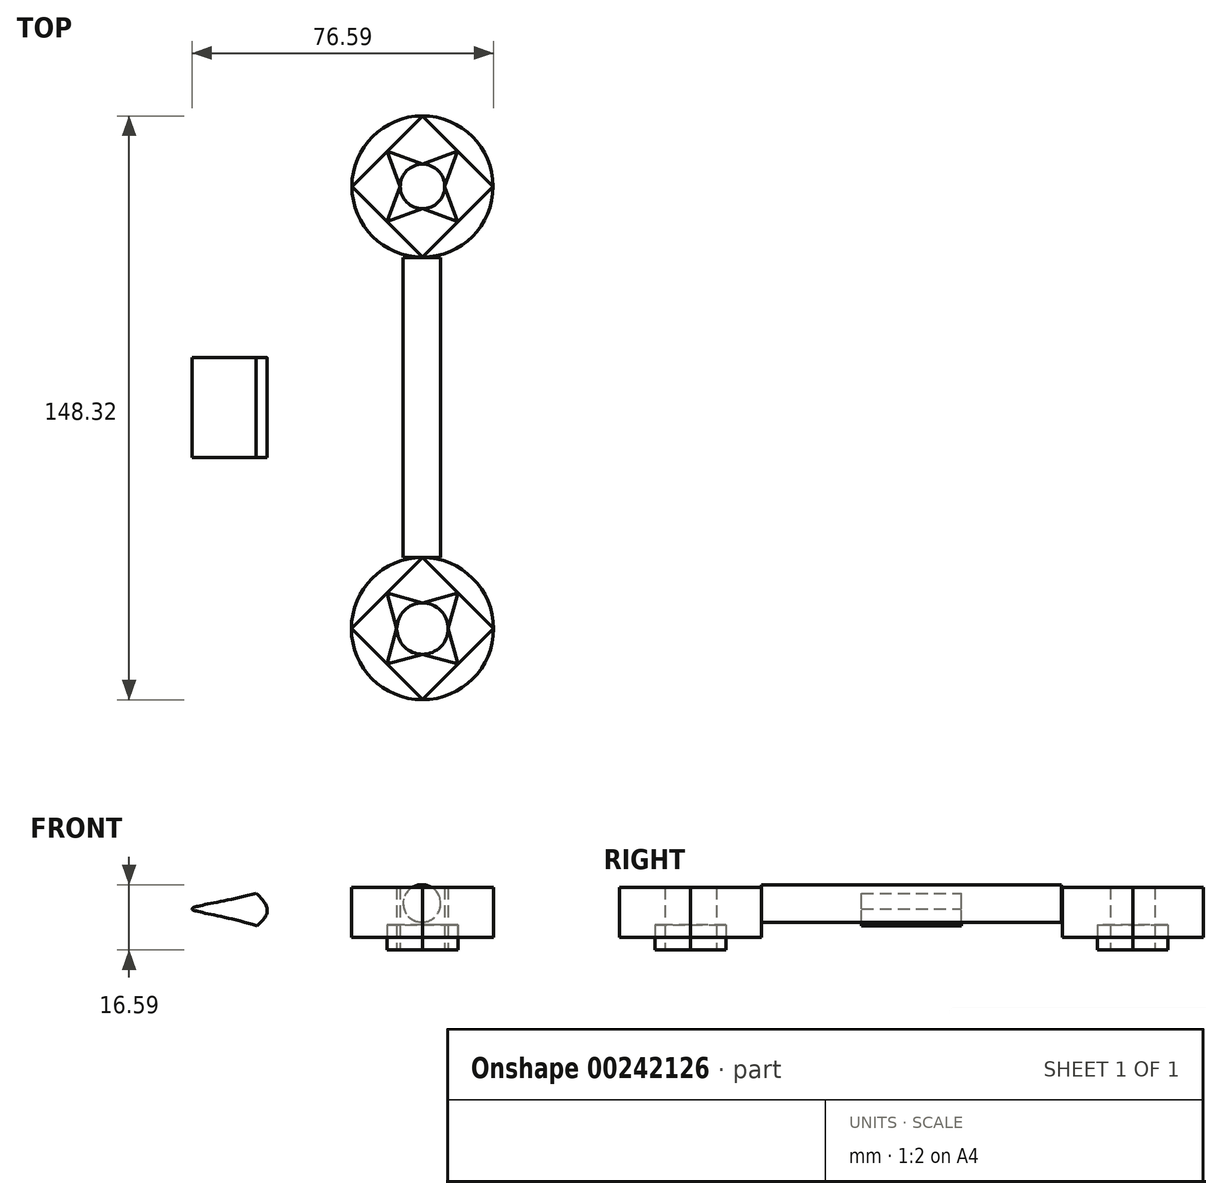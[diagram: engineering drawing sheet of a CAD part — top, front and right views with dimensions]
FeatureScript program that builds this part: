
annotation { "Feature Type Name" : "Feature", "Feature Type Description" : "" }
export const myFeature = defineFeature(function(context is Context, id is Id, definition is map)
    precondition{}
    {
        {
            var Q0;
            Q0=qCreatedBy(makeId("Front.planeOp"),FACE);
            var sketch = newSketch(context, id + "F0", { "sketchPlane" : qUnion([Q0])});
            skFitSpline(sketch, "E0", {"points": [v(6.44, 35.87) * mm, v(49.4, 8.94) * mm, v(5.1, -19.58) * mm, v(-25.43, 0) * mm, v(-49.02, 7.3) * mm, v(-21.3, 15.76) * mm, v(6.44, 35.87) * mm]});
            skFitSpline(sketch, "E1", {"points": [v(-32.74, 11.27) * mm, v(-66.44, 34.21) * mm, v(-49.02, 7.3) * mm, v(-67.58, -16.61) * mm, v(-32.56, 2.95) * mm, v(-32.74, 11.27) * mm]});
            skCircle(sketch, "E2", {"center": v(9.37, 8.66) * mm, "radius": 4.76 * mm});
            skSolve(sketch);
        }
        {
            var Q0;
            {var subQ1=sQuery(id+"F0.wireOp",EDGE,"E0");Q0=makeQuery(id+"F0.imprint","IMPRINT",FACE,{"disambiguationData":[TD([[makeQuery(id+"F0.imprint","IMPRINT",EDGE,{"derivedFrom":subQ1}),-1.0]])]});}
            extrude(context, id + "F1", {"entities" : qUnion([Q0]), "endBound" : BoundingType.SYMMETRIC, "depth" : 25.4 * mm});
        }
        {
            var Q0;
            Q0=makeQuery(id+"F0.imprint","IMPRINT",FACE,{"disambiguationData":[TD([[makeQuery(id+"F0.imprint","IMPRINT",EDGE,{"derivedFrom":sQuery(id+"F0.wireOp",EDGE,"E2")}),1.0]])]});
            extrude(context, id + "F2", {"entities" : qUnion([Q0]), "endBound" : BoundingType.SYMMETRIC, "depth" : 76.2 * mm});
        }
        {
            var Q0;
            Q0=qCreatedBy(makeId("Top.planeOp"),FACE);
            var sketch = newSketch(context, id + "F3", { "sketchPlane" : qUnion([Q0])});
            skCircle(sketch, "E3", {"center": v(9.51, -56.16) * mm, "radius": 18.06 * mm});
            skCircle(sketch, "E4", {"center": v(9.51, 56.18) * mm, "radius": 17.93 * mm});
            skLineSegment(sketch, "E5", {"start": v(-8.55, -56.16) * mm, "end": v(2.99, -56.16) * mm});
            skLineSegment(sketch, "E6", {"start": v(27.57, -56.16) * mm, "end": v(9.51, -74.22) * mm});
            skLineSegment(sketch, "E7", {"start": v(9.51, -74.22) * mm, "end": v(9.51, -62.69) * mm});
            skLineSegment(sketch, "E8", {"start": v(9.51, -38.1) * mm, "end": v(-8.55, -56.16) * mm});
            skLineSegment(sketch, "E9", {"start": v(9.51, -74.22) * mm, "end": v(-8.55, -56.16) * mm});
            skLineSegment(sketch, "E10", {"start": v(27.57, -56.16) * mm, "end": v(9.51, -38.1) * mm});
            skLineSegment(sketch, "E11", {"start": v(-8.41, 56.18) * mm, "end": v(3.85, 56.18) * mm});
            skLineSegment(sketch, "E12", {"start": v(9.51, 38.25) * mm, "end": v(9.51, 50.52) * mm});
            skLineSegment(sketch, "E13", {"start": v(9.51, 74.1) * mm, "end": v(-8.41, 56.18) * mm});
            skLineSegment(sketch, "E14", {"start": v(9.51, 38.25) * mm, "end": v(-8.41, 56.18) * mm});
            skLineSegment(sketch, "E15", {"start": v(9.51, 38.25) * mm, "end": v(27.44, 56.18) * mm});
            skLineSegment(sketch, "E16", {"start": v(9.51, 74.1) * mm, "end": v(27.44, 56.18) * mm});
            skCircle(sketch, "E17", {"center": v(9.51, -56.16) * mm, "radius": 6.53 * mm});
            skCircle(sketch, "E18", {"center": v(9.51, 56.18) * mm, "radius": 5.66 * mm});
            skLineSegment(sketch, "E19.trimOffspring", {"start": v(16.04, -56.16) * mm, "end": v(27.57, -56.16) * mm});
            skLineSegment(sketch, "E20.trimOffspring", {"start": v(9.51, -49.63) * mm, "end": v(9.51, -38.1) * mm});
            skLineSegment(sketch, "E21.trimOffspring", {"start": v(9.51, 61.83) * mm, "end": v(9.51, 74.1) * mm});
            skLineSegment(sketch, "E22.trimOffspring", {"start": v(15.17, 56.18) * mm, "end": v(27.44, 56.18) * mm});
            skLineSegment(sketch, "E23", {"start": v(3.85, 56.18) * mm, "end": v(0.55, 65.14) * mm});
            skLineSegment(sketch, "E24", {"start": v(0.55, 65.14) * mm, "end": v(9.51, 61.83) * mm});
            skLineSegment(sketch, "E25", {"start": v(9.51, 61.83) * mm, "end": v(18.48, 65.14) * mm});
            skLineSegment(sketch, "E26", {"start": v(18.48, 65.14) * mm, "end": v(15.17, 56.18) * mm});
            skLineSegment(sketch, "E27", {"start": v(15.17, 56.18) * mm, "end": v(18.48, 47.21) * mm});
            skLineSegment(sketch, "E28", {"start": v(18.48, 47.21) * mm, "end": v(9.51, 50.52) * mm});
            skLineSegment(sketch, "E29", {"start": v(3.85, 56.18) * mm, "end": v(0.55, 47.21) * mm});
            skLineSegment(sketch, "E30", {"start": v(0.55, 47.21) * mm, "end": v(9.51, 50.52) * mm});
            skLineSegment(sketch, "E31", {"start": v(2.99, -56.16) * mm, "end": v(0.48, -47.13) * mm});
            skLineSegment(sketch, "E32", {"start": v(0.48, -47.13) * mm, "end": v(9.51, -49.63) * mm});
            skLineSegment(sketch, "E33", {"start": v(9.51, -49.63) * mm, "end": v(18.54, -47.13) * mm});
            skLineSegment(sketch, "E34", {"start": v(18.54, -47.13) * mm, "end": v(16.04, -56.16) * mm});
            skLineSegment(sketch, "E35", {"start": v(16.04, -56.16) * mm, "end": v(18.54, -65.19) * mm});
            skLineSegment(sketch, "E36", {"start": v(18.54, -65.19) * mm, "end": v(9.51, -62.69) * mm});
            skLineSegment(sketch, "E37", {"start": v(9.51, -62.69) * mm, "end": v(0.48, -65.19) * mm});
            skLineSegment(sketch, "E38", {"start": v(0.48, -65.19) * mm, "end": v(2.99, -56.16) * mm});
            skSolve(sketch);
        }
        {
            var Q0;
            {var subQ0=sQuery(id+"F3.wireOp",EDGE,"E9");Q0=makeQuery(id+"F3.imprint","IMPRINT",FACE,{"disambiguationData":[TD([[makeQuery(id+"F3.imprint","IMPRINT",EDGE,{"derivedFrom":subQ0}),1.0]])]});}
            var Q1;
            {var subQ0=sQuery(id+"F3.wireOp",EDGE,"E8");Q1=makeQuery(id+"F3.imprint","IMPRINT",FACE,{"disambiguationData":[TD([[makeQuery(id+"F3.imprint","IMPRINT",EDGE,{"derivedFrom":subQ0}),-1.0]])]});}
            var Q2;
            {var subQ0=sQuery(id+"F3.wireOp",EDGE,"E6");Q2=makeQuery(id+"F3.imprint","IMPRINT",FACE,{"disambiguationData":[TD([[makeQuery(id+"F3.imprint","IMPRINT",EDGE,{"derivedFrom":subQ0}),1.0]])]});}
            var Q3;
            {var subQ0=sQuery(id+"F3.wireOp",EDGE,"E10");Q3=makeQuery(id+"F3.imprint","IMPRINT",FACE,{"disambiguationData":[TD([[makeQuery(id+"F3.imprint","IMPRINT",EDGE,{"derivedFrom":subQ0}),-1.0]])]});}
            var Q4;
            {var subQ0=sQuery(id+"F3.wireOp",EDGE,"E14");Q4=makeQuery(id+"F3.imprint","IMPRINT",FACE,{"disambiguationData":[TD([[makeQuery(id+"F3.imprint","IMPRINT",EDGE,{"derivedFrom":subQ0}),1.0]])]});}
            var Q5;
            {var subQ0=sQuery(id+"F3.wireOp",EDGE,"E13");Q5=makeQuery(id+"F3.imprint","IMPRINT",FACE,{"disambiguationData":[TD([[makeQuery(id+"F3.imprint","IMPRINT",EDGE,{"derivedFrom":subQ0}),-1.0]])]});}
            var Q6;
            {var subQ0=sQuery(id+"F3.wireOp",EDGE,"E16");Q6=makeQuery(id+"F3.imprint","IMPRINT",FACE,{"disambiguationData":[TD([[makeQuery(id+"F3.imprint","IMPRINT",EDGE,{"derivedFrom":subQ0}),1.0]])]});}
            var Q7;
            {var subQ0=sQuery(id+"F3.wireOp",EDGE,"E15");Q7=makeQuery(id+"F3.imprint","IMPRINT",FACE,{"disambiguationData":[TD([[makeQuery(id+"F3.imprint","IMPRINT",EDGE,{"derivedFrom":subQ0}),-1.0]])]});}
            var Q8;
            {var subQ0=sQuery(id+"F3.wireOp",EDGE,"E18");var subQ1=makeQuery(id+"F3.imprint","INTERSECT",VERTEX,{"derivedFrom":[subQ0,sQuery(id+"F3.wireOp",EDGE,"E21.trimOffspring")]});Q8=makeQuery(id+"F3.imprint","IMPRINT",FACE,{"disambiguationData":[TD([[makeQuery(id+"F3.imprint","IMPRINT",EDGE,{"disambiguationData":[TD([[subQ1,1.0]])],"derivedFrom":subQ0}),1.0]])]});}
            var Q9;
            {var subQ0=sQuery(id+"F3.wireOp",EDGE,"E17");var subQ1=makeQuery(id+"F3.imprint","INTERSECT",VERTEX,{"derivedFrom":[subQ0,sQuery(id+"F3.wireOp",EDGE,"E19.trimOffspring")]});Q9=makeQuery(id+"F3.imprint","IMPRINT",FACE,{"disambiguationData":[TD([[makeQuery(id+"F3.imprint","IMPRINT",EDGE,{"disambiguationData":[TD([[subQ1,-1.0]])],"derivedFrom":subQ0}),1.0]])]});}
            extrude(context, id + "F4", {"entities" : qUnion([Q0, Q1, Q2, Q3, Q4, Q5, Q6, Q7, Q8, Q9]), "depth" : 12.7 * mm});
        }
        {
            var Q0;
            {var subQ0=sQuery(id+"F3.wireOp",EDGE,"E31");Q0=makeQuery(id+"F3.imprint","IMPRINT",FACE,{"disambiguationData":[TD([[makeQuery(id+"F3.imprint","IMPRINT",EDGE,{"derivedFrom":subQ0}),-1.0]])]});}
            var Q1;
            {var subQ2=sQuery(id+"F3.wireOp",EDGE,"E33");Q1=makeQuery(id+"F3.imprint","IMPRINT",FACE,{"disambiguationData":[TD([[makeQuery(id+"F3.imprint","IMPRINT",EDGE,{"derivedFrom":subQ2}),-1.0]])]});}
            var Q2;
            {var subQ2=sQuery(id+"F3.wireOp",EDGE,"E35");Q2=makeQuery(id+"F3.imprint","IMPRINT",FACE,{"disambiguationData":[TD([[makeQuery(id+"F3.imprint","IMPRINT",EDGE,{"derivedFrom":subQ2}),-1.0]])]});}
            var Q3;
            {var subQ2=sQuery(id+"F3.wireOp",EDGE,"E37");Q3=makeQuery(id+"F3.imprint","IMPRINT",FACE,{"disambiguationData":[TD([[makeQuery(id+"F3.imprint","IMPRINT",EDGE,{"derivedFrom":subQ2}),-1.0]])]});}
            var Q4;
            {var subQ0=sQuery(id+"F3.wireOp",EDGE,"E29");Q4=makeQuery(id+"F3.imprint","IMPRINT",FACE,{"disambiguationData":[TD([[makeQuery(id+"F3.imprint","IMPRINT",EDGE,{"derivedFrom":subQ0}),1.0]])]});}
            var Q5;
            {var subQ0=sQuery(id+"F3.wireOp",EDGE,"E23");Q5=makeQuery(id+"F3.imprint","IMPRINT",FACE,{"disambiguationData":[TD([[makeQuery(id+"F3.imprint","IMPRINT",EDGE,{"derivedFrom":subQ0}),-1.0]])]});}
            var Q6;
            {var subQ0=sQuery(id+"F3.wireOp",EDGE,"E25");Q6=makeQuery(id+"F3.imprint","IMPRINT",FACE,{"disambiguationData":[TD([[makeQuery(id+"F3.imprint","IMPRINT",EDGE,{"derivedFrom":subQ0}),-1.0]])]});}
            var Q7;
            {var subQ2=sQuery(id+"F3.wireOp",EDGE,"E27");Q7=makeQuery(id+"F3.imprint","IMPRINT",FACE,{"disambiguationData":[TD([[makeQuery(id+"F3.imprint","IMPRINT",EDGE,{"derivedFrom":subQ2}),-1.0]])]});}
            extrude(context, id + "F5", {"entities" : qUnion([Q0, Q1, Q2, Q3, Q4, Q5, Q6, Q7]), "endBound" : BoundingType.SYMMETRIC, "depth" : 6.35 * mm});
        }
    });
